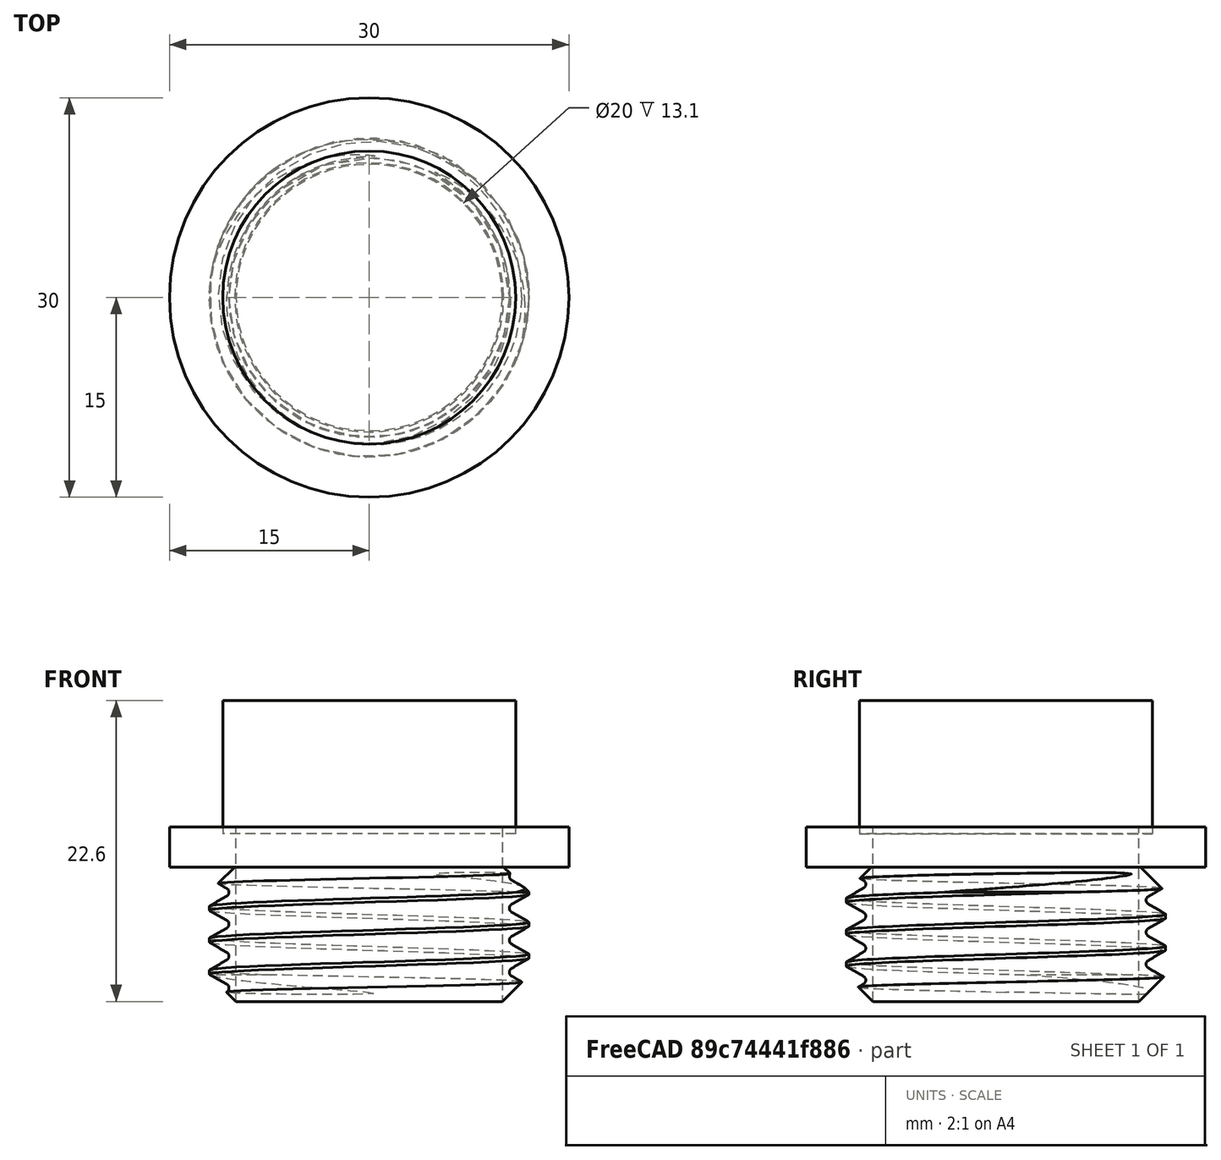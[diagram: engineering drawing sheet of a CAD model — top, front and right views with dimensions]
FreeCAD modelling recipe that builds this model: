
FCSTD DOCUMENT  (FreeCAD 1.0R39109 (Git))
Label: rosca_aspiradora
License: All rights reserved
LicenseURL: http://en.wikipedia.org/wiki/All_rights_reserved
objects: Sketcher::SketchObject×3, Part::FeaturePython×1, App::VarSet×1, PartDesign::FeatureBase×1, PartDesign::Pad×1, PartDesign::Pocket×1, PartDesign::Body×1, Part::Feature×1, Part::Cylinder×1, Mesh::Feature×1
note: 18 computed .brp shape members not serialized (recipe doc carries the construction recipe); baked Part::Feature solids carry a one-line shape summary decoded from their .brp

FEATURE [Part::FeaturePython] ThreadedRod  label="24x11-ThreadedRod"  # WARN: FeaturePython — macro-defined, semantics opaque (R4)
  Diameter = 29
  DiameterCustom = 24
  Invert = false
  LeftHanded = false
  Length = 11
  MatchOuter = false
  OffsetAngle = 0
  PitchCustom = 2.4
  Thread = true
  Type = 4
  expr: DiameterCustom = <<Threads>>.ThreadSize
FEATURE [App::VarSet] VarSet  label="Threads"
  ThreadSize = 24
FEATURE [PartDesign::FeatureBase] BaseFeature
  BaseFeature = -> ThreadedRod
  Suppressed = false
FEATURE [Sketcher::SketchObject] Sketch
  ArcFitTolerance = 1e-06
  AttachmentOffset = pos=(0,0,-0.5) rot=(0,0,1;0rad)
  AttachmentSupport = -> [BaseFeature]
  FullyConstrained = true
  MakeInternals = false
  MapMode = 5
  Placement = pos=(0,0,-0.5) rot=(0,0,1;0rad)
  sketch-geometry (1):
    g0: Circle CenterX=0 CenterY=0 CenterZ=0 NormalX=0 NormalY=0 NormalZ=1 AngleXU=0 Radius=15
  constraints (2):
    c: Diameter(g0) = 30
    c: Coincident(g0,g-1)
FEATURE [PartDesign::Pad] Pad
  BaseFeature = -> BaseFeature
  Direction = (0,0,1)
  Length = 3
  Length2 = 10
  Profile = -> Sketch
  ReferenceAxis = -> Sketch [N_Axis]
  Suppressed = false
  Type = 0
FEATURE [Sketcher::SketchObject] Sketch001
  ArcFitTolerance = 1e-06
  AttachmentSupport = -> [Pad]
  FullyConstrained = true
  MakeInternals = false
  MapMode = 5
  Placement = pos=(0,0,2.5) rot=(0,0,1;0rad)
  sketch-geometry (1):
    g0: Circle CenterX=0 CenterY=0 CenterZ=0 NormalX=0 NormalY=0 NormalZ=1 AngleXU=0 Radius=12.5
  constraints (2):
    c: Diameter(g0) = 25
    c: Coincident(g0,g-1)
FEATURE [Sketcher::SketchObject] Sketch002
  ArcFitTolerance = 1e-06
  AttachmentSupport = -> [Pad]
  FullyConstrained = true
  MakeInternals = false
  MapMode = 5
  Placement = pos=(0,0,2.5) rot=(0,0,1;0rad)
  sketch-geometry (1):
    g0: Circle CenterX=0 CenterY=0 CenterZ=0 NormalX=0 NormalY=0 NormalZ=1 AngleXU=0 Radius=10
  constraints (2):
    c: Diameter(g0) = 20
    c: Coincident(g0,g-1)
FEATURE [PartDesign::Pocket] Pocket
  BaseFeature = -> Pad
  Direction = (0,0,-1)
  Length = 5
  Length2 = 5
  Profile = -> Sketch002
  ReferenceAxis = -> Sketch002 [N_Axis]
  Suppressed = false
  Type = 1
FEATURE [PartDesign::Body] Body  label="Bolt"
  AllowCompound = false
  BaseFeature = -> ThreadedRod
  Group = -> [BaseFeature,Sketch,Pad,Sketch001,Sketch002,Pocket]
  Origin = -> Origin
  Tip = -> Pocket
FEATURE [Part::Feature] Pocket001
  shape: bbox 34.56 x 35.57 x 14.44 mm, 25 faces (baked)
FEATURE [Part::Cylinder] Cylinder
  Angle = 360
  AttacherType = Attacher::AttachEngine3D
  FirstAngle = 0
  Height = 10
  Placement = pos=(0,0,2) rot=(0,0,1;0rad)
  Radius = 11
  SecondAngle = 0
FEATURE [Mesh::Feature] Mesh  label="Pocket001 (Meshed)"
